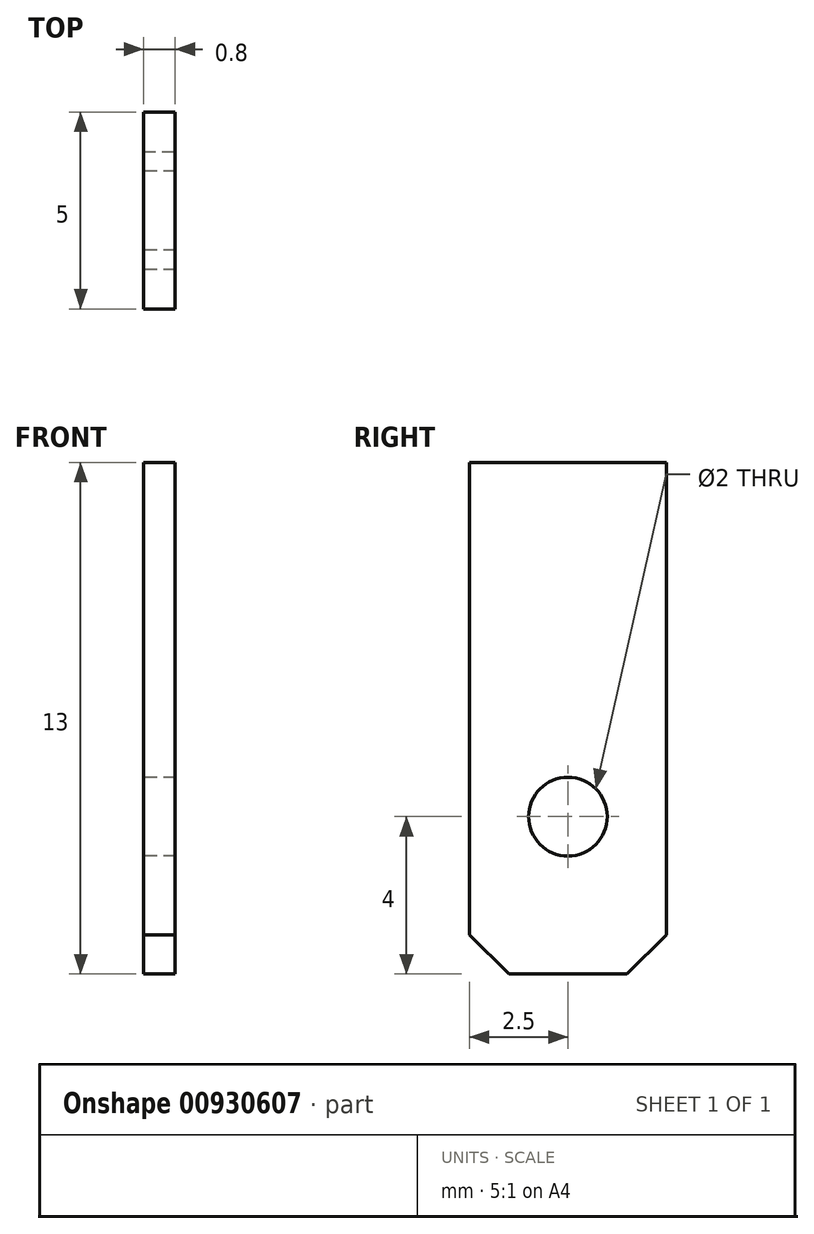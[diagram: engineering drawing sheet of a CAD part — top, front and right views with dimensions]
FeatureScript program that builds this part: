
annotation { "Feature Type Name" : "Feature", "Feature Type Description" : "" }
export const myFeature = defineFeature(function(context is Context, id is Id, definition is map)
    precondition{}
    {
        {
            var Q0;
            Q0=qCreatedBy(makeId("Top.planeOp"),FACE);
            var sketch = newSketch(context, id + "F0", { "sketchPlane" : qUnion([Q0])});
            skLineSegment(sketch, "E0.bottom", {"start": v(0, 0) * mm, "end": v(0.8, 0) * mm});
            skLineSegment(sketch, "E0.top", {"start": v(0, 5) * mm, "end": v(0.8, 5) * mm});
            skLineSegment(sketch, "E0.left", {"start": v(0, 0) * mm, "end": v(0, 5) * mm});
            skLineSegment(sketch, "E0.right", {"start": v(0.8, 0) * mm, "end": v(0.8, 5) * mm});
            skSolve(sketch);
        }
        {
            var Q0;
            Q0=qSketchRegion(id+"F0",true);
            extrude(context, id + "F1", {"entities" : qUnion([Q0]), "depth" : 13 * mm, "offsetDistance" : 25 * mm});
        }
        {
            var Q0;
            Q0=makeQuery(id+"F1.opExtrude","SWEPT_FACE",FACE,{"disambiguationData":[OSD([sQuery(id+"F0.wireOp",EDGE,"E0.left")])]});
            var sketch = newSketch(context, id + "F2", { "sketchPlane" : qUnion([Q0])});
            skCircle(sketch, "E1", {"center": v(-2.5, 4) * mm, "radius": 1 * mm});
            skLineSegment(sketch, "E2", {"start": v(-2.5, 13) * mm, "end": v(-2.5, 0) * mm, "construction": true});
            skSolve(sketch);
        }
        {
            var Q0;
            Q0=qSketchRegion(id+"F2",true);
            extrude(context, id + "F3", {"entities" : qUnion([Q0]), "operationType" : NewBodyOperationType.REMOVE, "endBound" : BoundingType.UP_TO_NEXT, "oppositeDirection" : true, "depth" : 25 * mm, "offsetDistance" : 25 * mm});
        }
        {
            var Q0;
            Q0=makeQuery(id+"F1.opExtrude","CAP_EDGE",EDGE,{"disambiguationData":[OSD([sQuery(id+"F0.wireOp",EDGE,"E0.top")])],"isStart":true});
            var Q1;
            Q1=makeQuery(id+"F1.opExtrude","CAP_EDGE",EDGE,{"disambiguationData":[OSD([sQuery(id+"F0.wireOp",EDGE,"E0.bottom")])],"isStart":true});
            chamfer(context, id + "F4", {"entities" : qUnion([Q0, Q1]), "width" : 1 * mm, "tangentPropagation" : true});
        }
    });
